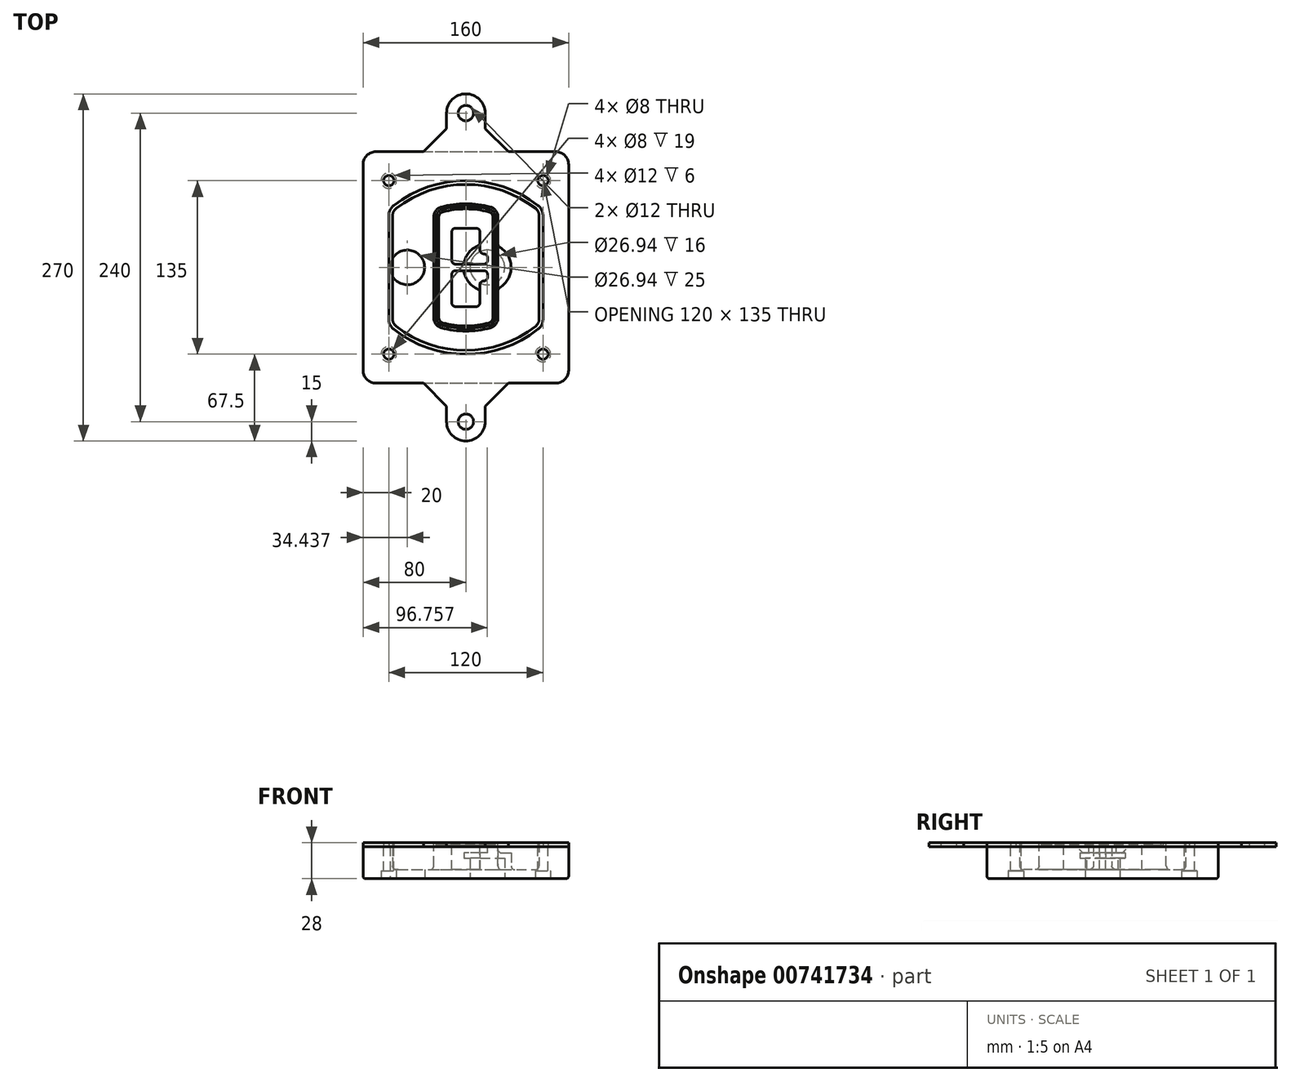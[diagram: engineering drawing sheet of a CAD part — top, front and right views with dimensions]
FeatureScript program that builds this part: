
annotation { "Feature Type Name" : "Feature", "Feature Type Description" : "" }
export const myFeature = defineFeature(function(context is Context, id is Id, definition is map)
    precondition{}
    {
        {
            var Q0;
            Q0=qCreatedBy(makeId("Top.planeOp"),FACE);
            var sketch = newSketch(context, id + "F0", { "sketchPlane" : qUnion([Q0])});
            skPoint(sketch, "E0.rect.middle", {"position": v(0, 0) * mm});
            skLineSegment(sketch, "E1.bottom", {"start": v(-70, -90) * mm, "end": v(70, -90) * mm});
            skLineSegment(sketch, "E1.top", {"start": v(-70, 90) * mm, "end": v(70, 90) * mm});
            skLineSegment(sketch, "E1.left", {"start": v(-80, -80) * mm, "end": v(-80, 80) * mm});
            skLineSegment(sketch, "E1.right", {"start": v(80, -80) * mm, "end": v(80, 80) * mm});
            skLineSegment(sketch, "E2", {"start": v(-80, 90) * mm, "end": v(80, -90) * mm, "construction": true});
            skLineSegment(sketch, "E3", {"start": v(80, 90) * mm, "end": v(-80, -90) * mm, "construction": true});
            skCircle(sketch, "E4", {"center": v(-60, 67.5) * mm, "radius": 4 * mm});
            skCircle(sketch, "E5", {"center": v(60, 67.5) * mm, "radius": 4 * mm});
            skCircle(sketch, "E6", {"center": v(60, -67.5) * mm, "radius": 4 * mm});
            skCircle(sketch, "E7", {"center": v(-60, -67.5) * mm, "radius": 4 * mm});
            skLineSegment(sketch, "E8", {"start": v(-60, 67.5) * mm, "end": v(60, 67.5) * mm, "construction": true});
            skLineSegment(sketch, "E9", {"start": v(60, 67.5) * mm, "end": v(60, -67.5) * mm, "construction": true});
            skLineSegment(sketch, "E10", {"start": v(60, -67.5) * mm, "end": v(-60, -67.5) * mm, "construction": true});
            skLineSegment(sketch, "E11", {"start": v(-60, -67.5) * mm, "end": v(-60, 67.5) * mm, "construction": true});
            skLineSegment(sketch, "E12", {"start": v(-60, 40.3) * mm, "end": v(-60, -40.3) * mm});
            skLineSegment(sketch, "E13", {"start": v(60, 40.3) * mm, "end": v(60, -40.3) * mm});
            skArc(sketch, "E14", {"start": v(56.15, 48.18) * mm, "mid": v(0, 67.5) * mm, "end": v(-56.15, 48.18) * mm});
            skArc(sketch, "E15", {"start": v(-56.15, -48.18) * mm, "mid": v(0, -67.5) * mm, "end": v(56.15, -48.18) * mm});
            skLineSegment(sketch, "E16", {"start": v(-60, 0) * mm, "end": v(60, 0) * mm, "construction": true});
            skPoint(sketch, "E17.visualSharp", {"position": v(-60, -45) * mm});
            skArc(sketch, "E17.filletArc", {"start": v(-60, -40.3) * mm, "mid": v(-58.99, -44.68) * mm, "end": v(-56.15, -48.18) * mm});
            skPoint(sketch, "E18.visualSharp", {"position": v(-60, 45) * mm});
            skArc(sketch, "E18.filletArc", {"start": v(-56.15, 48.18) * mm, "mid": v(-58.99, 44.68) * mm, "end": v(-60, 40.3) * mm});
            skPoint(sketch, "E19.visualSharp", {"position": v(60, 45) * mm});
            skArc(sketch, "E19.filletArc", {"start": v(60, 40.3) * mm, "mid": v(58.99, 44.68) * mm, "end": v(56.15, 48.18) * mm});
            skPoint(sketch, "E20.visualSharp", {"position": v(60, -45) * mm});
            skArc(sketch, "E20.filletArc", {"start": v(56.15, -48.18) * mm, "mid": v(58.99, -44.68) * mm, "end": v(60, -40.3) * mm});
            skPoint(sketch, "E21.visualSharp", {"position": v(-80, 90) * mm});
            skArc(sketch, "E21.filletArc", {"start": v(-70, 90) * mm, "mid": v(-77.07, 87.07) * mm, "end": v(-80, 80) * mm});
            skPoint(sketch, "E22.visualSharp", {"position": v(80, 90) * mm});
            skArc(sketch, "E22.filletArc", {"start": v(80, 80) * mm, "mid": v(77.07, 87.07) * mm, "end": v(70, 90) * mm});
            skPoint(sketch, "E23.visualSharp", {"position": v(80, -90) * mm});
            skArc(sketch, "E23.filletArc", {"start": v(70, -90) * mm, "mid": v(77.07, -87.07) * mm, "end": v(80, -80) * mm});
            skPoint(sketch, "E24.visualSharp", {"position": v(-80, -90) * mm});
            skArc(sketch, "E24.filletArc", {"start": v(-80, -80) * mm, "mid": v(-77.07, -87.07) * mm, "end": v(-70, -90) * mm});
            skArc(sketch, "E25.0", {"start": v(57, 40.3) * mm, "mid": v(56.3, 43.36) * mm, "end": v(54.3, 45.81) * mm});
            skLineSegment(sketch, "E25.1", {"start": v(57, 40.3) * mm, "end": v(57, -40.3) * mm});
            skArc(sketch, "E25.2", {"start": v(54.3, -45.81) * mm, "mid": v(56.3, -43.36) * mm, "end": v(57, -40.3) * mm});
            skArc(sketch, "E25.3", {"start": v(-54.3, -45.81) * mm, "mid": v(0, -64.5) * mm, "end": v(54.3, -45.81) * mm});
            skArc(sketch, "E25.4", {"start": v(-57, -40.3) * mm, "mid": v(-56.3, -43.36) * mm, "end": v(-54.3, -45.81) * mm});
            skArc(sketch, "E25.5", {"start": v(54.3, 45.81) * mm, "mid": v(0, 64.5) * mm, "end": v(-54.3, 45.81) * mm});
            skLineSegment(sketch, "E25.6", {"start": v(-57, 40.3) * mm, "end": v(-57, -40.3) * mm});
            skArc(sketch, "E25.7", {"start": v(-54.3, 45.81) * mm, "mid": v(-56.3, 43.36) * mm, "end": v(-57, 40.3) * mm});
            skArc(sketch, "E26.0", {"start": v(-58.62, 51.33) * mm, "mid": v(-62.58, 46.43) * mm, "end": v(-64, 40.3) * mm});
            skArc(sketch, "E26.1", {"start": v(58.62, 51.33) * mm, "mid": v(0, 71.5) * mm, "end": v(-58.62, 51.33) * mm});
            skArc(sketch, "E26.2", {"start": v(64, 40.3) * mm, "mid": v(62.58, 46.43) * mm, "end": v(58.62, 51.33) * mm});
            skLineSegment(sketch, "E26.3", {"start": v(64, 40.3) * mm, "end": v(64, -40.3) * mm});
            skArc(sketch, "E26.4", {"start": v(58.62, -51.33) * mm, "mid": v(62.58, -46.43) * mm, "end": v(64, -40.3) * mm});
            skLineSegment(sketch, "E26.5", {"start": v(-64, 40.3) * mm, "end": v(-64, -40.3) * mm});
            skArc(sketch, "E26.6", {"start": v(-58.62, -51.33) * mm, "mid": v(0, -71.5) * mm, "end": v(58.62, -51.33) * mm});
            skArc(sketch, "E26.7", {"start": v(-64, -40.3) * mm, "mid": v(-62.58, -46.43) * mm, "end": v(-58.62, -51.33) * mm});
            skSolve(sketch);
        }
        {
            var Q0;
            Q0=makeQuery(id+"F0.imprint","IMPRINT",FACE,{"disambiguationData":[TD([[makeQuery(id+"F0.imprint","IMPRINT",EDGE,{"derivedFrom":sQuery(id+"F0.wireOp",EDGE,"E1.bottom")}),1.0]])]});
            var Q1;
            Q1=makeQuery(id+"F0.imprint","IMPRINT",FACE,{"disambiguationData":[TD([[makeQuery(id+"F0.imprint","IMPRINT",EDGE,{"derivedFrom":sQuery(id+"F0.wireOp",EDGE,"E12")}),1.0]])]});
            var Q2;
            Q2=makeQuery(id+"F0.imprint","IMPRINT",FACE,{"disambiguationData":[TD([[makeQuery(id+"F0.imprint","IMPRINT",EDGE,{"derivedFrom":sQuery(id+"F0.wireOp",EDGE,"E25.0")}),1.0]])]});
            var Q3;
            Q3=makeQuery(id+"F0.imprint","IMPRINT",FACE,{"disambiguationData":[TD([[makeQuery(id+"F0.imprint","IMPRINT",EDGE,{"derivedFrom":sQuery(id+"F0.wireOp",EDGE,"E12")}),-1.0]])]});
            extrude(context, id + "F1", {"entities" : qUnion([Q0, Q1, Q2, Q3]), "oppositeDirection" : true, "depth" : 25 * mm});
        }
        {
            var Q0;
            Q0=makeQuery(id+"F0.imprint","IMPRINT",FACE,{"disambiguationData":[TD([[makeQuery(id+"F0.imprint","IMPRINT",EDGE,{"derivedFrom":sQuery(id+"F0.wireOp",EDGE,"E12")}),1.0]])]});
            extrude(context, id + "F2", {"entities" : qUnion([Q0]), "operationType" : NewBodyOperationType.ADD, "depth" : 3 * mm});
        }
        {
            var Q0;
            Q0=makeQuery(id+"F0.imprint","IMPRINT",FACE,{"disambiguationData":[TD([[makeQuery(id+"F0.imprint","IMPRINT",EDGE,{"derivedFrom":sQuery(id+"F0.wireOp",EDGE,"E25.0")}),1.0]])]});
            extrude(context, id + "F3", {"entities" : qUnion([Q0]), "operationType" : NewBodyOperationType.REMOVE, "oppositeDirection" : true, "depth" : 18 * mm});
        }
        {
            var Q0;
            Q0=makeQuery(id+"F2.opExtrude","CAP_FACE",FACE,{"disambiguationData":[OSD([sQuery(id+"F0.wireOp",EDGE,"E12"),sQuery(id+"F0.wireOp",EDGE,"E13"),sQuery(id+"F0.wireOp",EDGE,"E14"),sQuery(id+"F0.wireOp",EDGE,"E15"),sQuery(id+"F0.wireOp",EDGE,"E17.filletArc"),sQuery(id+"F0.wireOp",EDGE,"E18.filletArc"),sQuery(id+"F0.wireOp",EDGE,"E19.filletArc"),sQuery(id+"F0.wireOp",EDGE,"E20.filletArc"),sQuery(id+"F0.wireOp",EDGE,"E25.0"),sQuery(id+"F0.wireOp",EDGE,"E25.1"),sQuery(id+"F0.wireOp",EDGE,"E25.2"),sQuery(id+"F0.wireOp",EDGE,"E25.3"),sQuery(id+"F0.wireOp",EDGE,"E25.4"),sQuery(id+"F0.wireOp",EDGE,"E25.5"),sQuery(id+"F0.wireOp",EDGE,"E25.6"),sQuery(id+"F0.wireOp",EDGE,"E25.7")])],"isStart":false});
            var sketch = newSketch(context, id + "F4", { "sketchPlane" : qUnion([Q0])});
            skArc(sketch, "E27.0", {"start": v(-19.08, -46.97) * mm, "mid": v(0, -49.5) * mm, "end": v(19.08, -46.97) * mm});
            skArc(sketch, "E28.0", {"start": v(19.08, 46.97) * mm, "mid": v(0, 49.5) * mm, "end": v(-19.08, 46.97) * mm});
            skLineSegment(sketch, "E29", {"start": v(-25, 39.25) * mm, "end": v(-25, -39.25) * mm});
            skLineSegment(sketch, "E30", {"start": v(25, 39.25) * mm, "end": v(25, -39.25) * mm});
            skLineSegment(sketch, "E31", {"start": v(-25, 45.1) * mm, "end": v(25, 45.1) * mm, "construction": true});
            skLineSegment(sketch, "E32", {"start": v(-25, -45.1) * mm, "end": v(25, -45.1) * mm, "construction": true});
            skPoint(sketch, "E33.visualSharp", {"position": v(-25, 45.1) * mm});
            skArc(sketch, "E33.filletArc", {"start": v(-19.08, 46.97) * mm, "mid": v(-23.35, 44.11) * mm, "end": v(-25, 39.25) * mm});
            skPoint(sketch, "E34.visualSharp", {"position": v(25, 45.1) * mm});
            skArc(sketch, "E34.filletArc", {"start": v(25, 39.25) * mm, "mid": v(23.35, 44.11) * mm, "end": v(19.08, 46.97) * mm});
            skPoint(sketch, "E35.visualSharp", {"position": v(25, -45.1) * mm});
            skArc(sketch, "E35.filletArc", {"start": v(19.08, -46.97) * mm, "mid": v(23.35, -44.11) * mm, "end": v(25, -39.25) * mm});
            skPoint(sketch, "E36.visualSharp", {"position": v(-25, -45.1) * mm});
            skArc(sketch, "E36.filletArc", {"start": v(-25, -39.25) * mm, "mid": v(-23.35, -44.11) * mm, "end": v(-19.08, -46.97) * mm});
            skArc(sketch, "E37.0", {"start": v(54.3, 45.81) * mm, "mid": v(0, 64.5) * mm, "end": v(-54.3, 45.81) * mm});
            skArc(sketch, "E37.1", {"start": v(-54.3, 45.81) * mm, "mid": v(-56.3, 43.36) * mm, "end": v(-57, 40.3) * mm});
            skLineSegment(sketch, "E37.2", {"start": v(-57, 40.3) * mm, "end": v(-57, -40.3) * mm});
            skArc(sketch, "E37.3", {"start": v(-57, -40.3) * mm, "mid": v(-56.3, -43.36) * mm, "end": v(-54.3, -45.81) * mm});
            skArc(sketch, "E37.4", {"start": v(-54.3, -45.81) * mm, "mid": v(0, -64.5) * mm, "end": v(54.3, -45.81) * mm});
            skArc(sketch, "E37.5", {"start": v(54.3, -45.81) * mm, "mid": v(56.3, -43.36) * mm, "end": v(57, -40.3) * mm});
            skLineSegment(sketch, "E37.6", {"start": v(57, 40.3) * mm, "end": v(57, -40.3) * mm});
            skArc(sketch, "E37.7", {"start": v(57, 40.3) * mm, "mid": v(56.3, 43.36) * mm, "end": v(54.3, 45.81) * mm});
            skLineSegment(sketch, "E38.0", {"start": v(23, 39.25) * mm, "end": v(23, -39.25) * mm});
            skArc(sketch, "E38.1", {"start": v(18.56, -45.04) * mm, "mid": v(21.76, -42.9) * mm, "end": v(23, -39.25) * mm});
            skArc(sketch, "E38.2", {"start": v(-18.56, -45.04) * mm, "mid": v(0, -47.5) * mm, "end": v(18.56, -45.04) * mm});
            skArc(sketch, "E38.3", {"start": v(-23, -39.25) * mm, "mid": v(-21.76, -42.9) * mm, "end": v(-18.56, -45.04) * mm});
            skLineSegment(sketch, "E38.4", {"start": v(-23, 39.25) * mm, "end": v(-23, -39.25) * mm});
            skArc(sketch, "E38.5", {"start": v(23, 39.25) * mm, "mid": v(21.76, 42.9) * mm, "end": v(18.56, 45.04) * mm});
            skArc(sketch, "E38.6", {"start": v(-18.56, 45.04) * mm, "mid": v(-21.76, 42.9) * mm, "end": v(-23, 39.25) * mm});
            skArc(sketch, "E38.7", {"start": v(18.56, 45.04) * mm, "mid": v(0, 47.5) * mm, "end": v(-18.56, 45.04) * mm});
            skArc(sketch, "E39.0", {"start": v(21, 39.25) * mm, "mid": v(20.18, 41.68) * mm, "end": v(18.04, 43.1) * mm});
            skLineSegment(sketch, "E39.1", {"start": v(21, 39.25) * mm, "end": v(21, -39.25) * mm});
            skArc(sketch, "E39.2", {"start": v(18.04, -43.1) * mm, "mid": v(20.18, -41.68) * mm, "end": v(21, -39.25) * mm});
            skArc(sketch, "E39.3", {"start": v(-18.04, -43.1) * mm, "mid": v(0, -45.5) * mm, "end": v(18.04, -43.1) * mm});
            skArc(sketch, "E39.4", {"start": v(-21, -39.25) * mm, "mid": v(-20.18, -41.68) * mm, "end": v(-18.04, -43.1) * mm});
            skArc(sketch, "E39.5", {"start": v(18.04, 43.1) * mm, "mid": v(0, 45.5) * mm, "end": v(-18.04, 43.1) * mm});
            skLineSegment(sketch, "E39.6", {"start": v(-21, 39.25) * mm, "end": v(-21, -39.25) * mm});
            skArc(sketch, "E39.7", {"start": v(-18.04, 43.1) * mm, "mid": v(-20.18, 41.68) * mm, "end": v(-21, 39.25) * mm});
            skLineSegment(sketch, "E40", {"start": v(-25, 0) * mm, "end": v(25, 0) * mm, "construction": true});
            skLineSegment(sketch, "E41", {"start": v(-11, 5.5) * mm, "end": v(-11, 27.5) * mm});
            skLineSegment(sketch, "E42", {"start": v(-8, 30.5) * mm, "end": v(8, 30.5) * mm});
            skLineSegment(sketch, "E43", {"start": v(11, 27.5) * mm, "end": v(11, 13.5) * mm});
            skLineSegment(sketch, "E44", {"start": v(14, 10.5) * mm, "end": v(14, 10.5) * mm});
            skLineSegment(sketch, "E45", {"start": v(17, 7.5) * mm, "end": v(17, 5.5) * mm});
            skLineSegment(sketch, "E46", {"start": v(14, 2.5) * mm, "end": v(-8, 2.5) * mm});
            skPoint(sketch, "E47.visualSharp", {"position": v(-11, 30.5) * mm});
            skArc(sketch, "E47.filletArc", {"start": v(-8, 30.5) * mm, "mid": v(-10.12, 29.62) * mm, "end": v(-11, 27.5) * mm});
            skPoint(sketch, "E48.visualSharp", {"position": v(11, 30.5) * mm});
            skArc(sketch, "E48.filletArc", {"start": v(11, 27.5) * mm, "mid": v(10.12, 29.62) * mm, "end": v(8, 30.5) * mm});
            skPoint(sketch, "E49.visualSharp", {"position": v(11, 10.5) * mm});
            skArc(sketch, "E49.filletArc", {"start": v(11, 13.5) * mm, "mid": v(11.88, 11.38) * mm, "end": v(14, 10.5) * mm});
            skPoint(sketch, "E50.visualSharp", {"position": v(17, 10.5) * mm});
            skArc(sketch, "E50.filletArc", {"start": v(17, 7.5) * mm, "mid": v(16.12, 9.62) * mm, "end": v(14, 10.5) * mm});
            skPoint(sketch, "E51.visualSharp", {"position": v(17, 2.5) * mm});
            skArc(sketch, "E51.filletArc", {"start": v(14, 2.5) * mm, "mid": v(16.12, 3.38) * mm, "end": v(17, 5.5) * mm});
            skPoint(sketch, "E52.visualSharp", {"position": v(-11, 2.5) * mm});
            skArc(sketch, "E52.filletArc", {"start": v(-11, 5.5) * mm, "mid": v(-10.12, 3.38) * mm, "end": v(-8, 2.5) * mm});
            skLineSegment(sketch, "E53.0.MirrorCS", {"start": v(14, -2.5) * mm, "end": v(-8, -2.5) * mm});
            skArc(sketch, "E54.0.MirrorCS", {"start": v(-11, -5.5) * mm, "mid": v(-10.12, -3.38) * mm, "end": v(-8, -2.5) * mm});
            skLineSegment(sketch, "E55.0.MirrorCS", {"start": v(-11, -5.5) * mm, "end": v(-11, -27.5) * mm});
            skArc(sketch, "E56.0.MirrorCS", {"start": v(-8, -30.5) * mm, "mid": v(-10.12, -29.62) * mm, "end": v(-11, -27.5) * mm});
            skLineSegment(sketch, "E57.0.MirrorCS", {"start": v(-8, -30.5) * mm, "end": v(8, -30.5) * mm});
            skArc(sketch, "E58.0.MirrorCS", {"start": v(11, -27.5) * mm, "mid": v(10.12, -29.62) * mm, "end": v(8, -30.5) * mm});
            skLineSegment(sketch, "E59.0.MirrorCS", {"start": v(11, -27.5) * mm, "end": v(11, -13.5) * mm});
            skArc(sketch, "E60.0.MirrorCS", {"start": v(11, -13.5) * mm, "mid": v(11.88, -11.38) * mm, "end": v(14, -10.5) * mm});
            skArc(sketch, "E61.0.MirrorCS", {"start": v(17, -7.5) * mm, "mid": v(16.12, -9.62) * mm, "end": v(14, -10.5) * mm});
            skLineSegment(sketch, "E62.0.MirrorCS", {"start": v(17, -7.5) * mm, "end": v(17, -5.5) * mm});
            skArc(sketch, "E63.0.MirrorCS", {"start": v(14, -2.5) * mm, "mid": v(16.12, -3.38) * mm, "end": v(17, -5.5) * mm});
            skSolve(sketch);
        }
        {
            var Q0;
            Q0=makeQuery(id+"F4.imprint","IMPRINT",FACE,{"disambiguationData":[TD([[makeQuery(id+"F4.imprint","IMPRINT",EDGE,{"derivedFrom":sQuery(id+"F4.wireOp",EDGE,"E27.0")}),1.0]])]});
            var Q1;
            Q1=makeQuery(id+"F4.imprint","IMPRINT",FACE,{"disambiguationData":[TD([[makeQuery(id+"F4.imprint","IMPRINT",EDGE,{"derivedFrom":sQuery(id+"F4.wireOp",EDGE,"E38.0")}),-1.0]])]});
            var Q2;
            Q2=makeQuery(id+"F4.imprint","IMPRINT",FACE,{"disambiguationData":[TD([[makeQuery(id+"F4.imprint","IMPRINT",EDGE,{"derivedFrom":sQuery(id+"F4.wireOp",EDGE,"E39.0")}),1.0]])]});
            extrude(context, id + "F5", {"entities" : qUnion([Q0, Q1, Q2]), "operationType" : NewBodyOperationType.ADD, "endBound" : BoundingType.UP_TO_NEXT, "oppositeDirection" : true, "depth" : 25 * mm});
        }
        {
            var Q0;
            Q0=makeQuery(id+"F4.imprint","IMPRINT",FACE,{"disambiguationData":[TD([[makeQuery(id+"F4.imprint","IMPRINT",EDGE,{"derivedFrom":sQuery(id+"F4.wireOp",EDGE,"E38.0")}),-1.0]])]});
            extrude(context, id + "F6", {"entities" : qUnion([Q0]), "operationType" : NewBodyOperationType.REMOVE, "oppositeDirection" : true, "depth" : 2 * mm});
        }
        {
            var Q0;
            Q0=makeQuery(id+"F1.opExtrude","CAP_FACE",FACE,{"disambiguationData":[OSD([sQuery(id+"F0.wireOp",EDGE,"E1.bottom"),sQuery(id+"F0.wireOp",EDGE,"E1.top"),sQuery(id+"F0.wireOp",EDGE,"E1.left"),sQuery(id+"F0.wireOp",EDGE,"E1.right"),sQuery(id+"F0.wireOp",EDGE,"E4"),sQuery(id+"F0.wireOp",EDGE,"E5"),sQuery(id+"F0.wireOp",EDGE,"E6"),sQuery(id+"F0.wireOp",EDGE,"E7"),sQuery(id+"F0.wireOp",EDGE,"E21.filletArc"),sQuery(id+"F0.wireOp",EDGE,"E22.filletArc"),sQuery(id+"F0.wireOp",EDGE,"E23.filletArc"),sQuery(id+"F0.wireOp",EDGE,"E24.filletArc")])],"isStart":false});
            var sketch = newSketch(context, id + "F7", { "sketchPlane" : qUnion([Q0])});
            skCircle(sketch, "E64", {"center": v(16.76, 0) * mm, "radius": 13.47 * mm});
            skCircle(sketch, "E65", {"center": v(-45.56, 0) * mm, "radius": 13.47 * mm});
            skLineSegment(sketch, "E66", {"start": v(80, 0) * mm, "end": v(-80, 0) * mm});
            skCircle(sketch, "E67", {"center": v(16.76, 0) * mm, "radius": 18.47 * mm});
            skCircle(sketch, "E68", {"center": v(60, -67.5) * mm, "radius": 6 * mm});
            skCircle(sketch, "E69", {"center": v(-60, -67.5) * mm, "radius": 6 * mm});
            skCircle(sketch, "E70", {"center": v(-60, 67.5) * mm, "radius": 6 * mm});
            skCircle(sketch, "E71", {"center": v(60, 67.5) * mm, "radius": 6 * mm});
            skSolve(sketch);
        }
        {
            var Q0;
            {var subQ1=sQuery(id+"F7.wireOp",EDGE,"E66");var subQ4=sQuery(id+"F7.wireOp",EDGE,"E64");var subQ6=makeQuery(id+"F7.imprint","INTERSECT",VERTEX,{"disambiguationData":[OD(0.0)],"derivedFrom":[subQ4,subQ1]});Q0=makeQuery(id+"F7.imprint","IMPRINT",FACE,{"disambiguationData":[TD([[makeQuery(id+"F7.imprint","IMPRINT",EDGE,{"disambiguationData":[TD([[subQ6,-1.0]])],"derivedFrom":subQ4}),-1.0]])]});}
            var Q1;
            {var subQ0=sQuery(id+"F7.wireOp",EDGE,"E66");var subQ1=sQuery(id+"F7.wireOp",EDGE,"E64");var subQ3=makeQuery(id+"F7.imprint","INTERSECT",VERTEX,{"disambiguationData":[OD(0.0)],"derivedFrom":[subQ1,subQ0]});Q1=makeQuery(id+"F7.imprint","IMPRINT",FACE,{"disambiguationData":[TD([[makeQuery(id+"F7.imprint","IMPRINT",EDGE,{"disambiguationData":[TD([[subQ3,-1.0]])],"derivedFrom":subQ1}),1.0]])]});}
            var Q2;
            {var subQ0=sQuery(id+"F7.wireOp",EDGE,"E66");var subQ1=sQuery(id+"F7.wireOp",EDGE,"E64");var subQ3=makeQuery(id+"F7.imprint","INTERSECT",VERTEX,{"disambiguationData":[OD(0.0)],"derivedFrom":[subQ1,subQ0]});Q2=makeQuery(id+"F7.imprint","IMPRINT",FACE,{"disambiguationData":[TD([[makeQuery(id+"F7.imprint","IMPRINT",EDGE,{"disambiguationData":[TD([[subQ3,1.0]])],"derivedFrom":subQ1}),1.0]])]});}
            var Q3;
            {var subQ1=sQuery(id+"F7.wireOp",EDGE,"E66");var subQ4=sQuery(id+"F7.wireOp",EDGE,"E64");var subQ6=makeQuery(id+"F7.imprint","INTERSECT",VERTEX,{"disambiguationData":[OD(0.0)],"derivedFrom":[subQ4,subQ1]});Q3=makeQuery(id+"F7.imprint","IMPRINT",FACE,{"disambiguationData":[TD([[makeQuery(id+"F7.imprint","IMPRINT",EDGE,{"disambiguationData":[TD([[subQ6,1.0]])],"derivedFrom":subQ4}),-1.0]])]});}
            extrude(context, id + "F8", {"entities" : qUnion([Q0, Q1, Q2, Q3]), "operationType" : NewBodyOperationType.ADD, "oppositeDirection" : true, "depth" : 20 * mm});
        }
        {
            var Q0;
            {var subQ0=sQuery(id+"F7.wireOp",EDGE,"E66");var subQ1=sQuery(id+"F7.wireOp",EDGE,"E64");var subQ3=makeQuery(id+"F7.imprint","INTERSECT",VERTEX,{"disambiguationData":[OD(0.0)],"derivedFrom":[subQ1,subQ0]});Q0=makeQuery(id+"F7.imprint","IMPRINT",FACE,{"disambiguationData":[TD([[makeQuery(id+"F7.imprint","IMPRINT",EDGE,{"disambiguationData":[TD([[subQ3,-1.0]])],"derivedFrom":subQ1}),1.0]])]});}
            var Q1;
            {var subQ0=sQuery(id+"F7.wireOp",EDGE,"E66");var subQ1=sQuery(id+"F7.wireOp",EDGE,"E64");var subQ3=makeQuery(id+"F7.imprint","INTERSECT",VERTEX,{"disambiguationData":[OD(0.0)],"derivedFrom":[subQ1,subQ0]});Q1=makeQuery(id+"F7.imprint","IMPRINT",FACE,{"disambiguationData":[TD([[makeQuery(id+"F7.imprint","IMPRINT",EDGE,{"disambiguationData":[TD([[subQ3,1.0]])],"derivedFrom":subQ1}),1.0]])]});}
            extrude(context, id + "F9", {"entities" : qUnion([Q0, Q1]), "operationType" : NewBodyOperationType.REMOVE, "oppositeDirection" : true, "depth" : 16 * mm});
        }
        {
            var Q0;
            {var subQ0=sQuery(id+"F7.wireOp",EDGE,"E66");var subQ1=sQuery(id+"F7.wireOp",EDGE,"E65");var subQ3=makeQuery(id+"F7.imprint","INTERSECT",VERTEX,{"disambiguationData":[OD(0.0)],"derivedFrom":[subQ1,subQ0]});Q0=makeQuery(id+"F7.imprint","IMPRINT",FACE,{"disambiguationData":[TD([[makeQuery(id+"F7.imprint","IMPRINT",EDGE,{"disambiguationData":[TD([[subQ3,-1.0]])],"derivedFrom":subQ1}),1.0]])]});}
            var Q1;
            {var subQ0=sQuery(id+"F7.wireOp",EDGE,"E66");var subQ1=sQuery(id+"F7.wireOp",EDGE,"E65");var subQ3=makeQuery(id+"F7.imprint","INTERSECT",VERTEX,{"disambiguationData":[OD(0.0)],"derivedFrom":[subQ1,subQ0]});Q1=makeQuery(id+"F7.imprint","IMPRINT",FACE,{"disambiguationData":[TD([[makeQuery(id+"F7.imprint","IMPRINT",EDGE,{"disambiguationData":[TD([[subQ3,1.0]])],"derivedFrom":subQ1}),1.0]])]});}
            extrude(context, id + "F10", {"entities" : qUnion([Q0, Q1]), "operationType" : NewBodyOperationType.REMOVE, "oppositeDirection" : true, "depth" : 25 * mm});
        }
        {
            var Q0;
            Q0=makeQuery(id+"F7.imprint","IMPRINT",FACE,{"disambiguationData":[TD([[makeQuery(id+"F7.imprint","IMPRINT",EDGE,{"derivedFrom":sQuery(id+"F7.wireOp",EDGE,"E68")}),1.0]])]});
            var Q1;
            Q1=makeQuery(id+"F7.imprint","IMPRINT",FACE,{"disambiguationData":[TD([[makeQuery(id+"F7.imprint","IMPRINT",EDGE,{"derivedFrom":makeQuery(id+"F1.opExtrude","CAP_EDGE",EDGE,{"disambiguationData":[OSD([sQuery(id+"F0.wireOp",EDGE,"E5")])],"isStart":false})}),-1.0]])]});
            var Q2;
            Q2=makeQuery(id+"F7.imprint","IMPRINT",FACE,{"disambiguationData":[TD([[makeQuery(id+"F7.imprint","IMPRINT",EDGE,{"derivedFrom":sQuery(id+"F7.wireOp",EDGE,"E69")}),1.0]])]});
            var Q3;
            Q3=makeQuery(id+"F7.imprint","IMPRINT",FACE,{"disambiguationData":[TD([[makeQuery(id+"F7.imprint","IMPRINT",EDGE,{"derivedFrom":makeQuery(id+"F1.opExtrude","CAP_EDGE",EDGE,{"disambiguationData":[OSD([sQuery(id+"F0.wireOp",EDGE,"E4")])],"isStart":false})}),-1.0]])]});
            var Q4;
            Q4=makeQuery(id+"F7.imprint","IMPRINT",FACE,{"disambiguationData":[TD([[makeQuery(id+"F7.imprint","IMPRINT",EDGE,{"derivedFrom":sQuery(id+"F7.wireOp",EDGE,"E70")}),1.0]])]});
            var Q5;
            Q5=makeQuery(id+"F7.imprint","IMPRINT",FACE,{"disambiguationData":[TD([[makeQuery(id+"F7.imprint","IMPRINT",EDGE,{"derivedFrom":makeQuery(id+"F1.opExtrude","CAP_EDGE",EDGE,{"disambiguationData":[OSD([sQuery(id+"F0.wireOp",EDGE,"E7")])],"isStart":false})}),-1.0]])]});
            var Q6;
            Q6=makeQuery(id+"F7.imprint","IMPRINT",FACE,{"disambiguationData":[TD([[makeQuery(id+"F7.imprint","IMPRINT",EDGE,{"derivedFrom":sQuery(id+"F7.wireOp",EDGE,"E71")}),1.0]])]});
            var Q7;
            Q7=makeQuery(id+"F7.imprint","IMPRINT",FACE,{"disambiguationData":[TD([[makeQuery(id+"F7.imprint","IMPRINT",EDGE,{"derivedFrom":makeQuery(id+"F1.opExtrude","CAP_EDGE",EDGE,{"disambiguationData":[OSD([sQuery(id+"F0.wireOp",EDGE,"E6")])],"isStart":false})}),-1.0]])]});
            extrude(context, id + "F11", {"entities" : qUnion([Q0, Q1, Q2, Q3, Q4, Q5, Q6, Q7]), "operationType" : NewBodyOperationType.REMOVE, "oppositeDirection" : true, "depth" : 6 * mm});
        }
        {
            var Q0;
            Q0=makeQuery(id+"F9.boolean.opBoolean","COPY",FACE,{"derivedFrom":makeQuery(id+"F9.opExtrude","CAP_FACE",FACE,{"disambiguationData":[OSD([sQuery(id+"F7.wireOp",EDGE,"E64")])],"isStart":false})});
            var sketch = newSketch(context, id + "F12", { "sketchPlane" : qUnion([Q0])});
            skArc(sketch, "E72.0", {"start": v(11, 17.55) * mm, "mid": v(2.57, 11.82) * mm, "end": v(-1.54, 2.5) * mm});
            skArc(sketch, "E72.1", {"start": v(-1.54, -2.5) * mm, "mid": v(2.57, -11.82) * mm, "end": v(11, -17.55) * mm});
            skLineSegment(sketch, "E73", {"start": v(-1.54, -2.5) * mm, "end": v(14, -2.5) * mm});
            skLineSegment(sketch, "E74.0", {"start": v(14, 2.5) * mm, "end": v(-1.54, 2.5) * mm});
            skArc(sketch, "E74.1", {"start": v(14, 2.5) * mm, "mid": v(16.12, 3.38) * mm, "end": v(17, 5.5) * mm});
            skLineSegment(sketch, "E74.2", {"start": v(17, 7.5) * mm, "end": v(17, 5.5) * mm});
            skArc(sketch, "E74.3", {"start": v(17, 7.5) * mm, "mid": v(16.12, 9.62) * mm, "end": v(14, 10.5) * mm});
            skArc(sketch, "E74.4", {"start": v(11, 13.5) * mm, "mid": v(11.88, 11.38) * mm, "end": v(14, 10.5) * mm});
            skLineSegment(sketch, "E74.5", {"start": v(11, 17.55) * mm, "end": v(11, 13.5) * mm});
            skLineSegment(sketch, "E74.7", {"start": v(14, -2.5) * mm, "end": v(-1.54, -2.5) * mm});
            skArc(sketch, "E74.8", {"start": v(14, -2.5) * mm, "mid": v(16.12, -3.38) * mm, "end": v(17, -5.5) * mm});
            skLineSegment(sketch, "E74.9", {"start": v(17, -7.5) * mm, "end": v(17, -5.5) * mm});
            skArc(sketch, "E74.10", {"start": v(17, -7.5) * mm, "mid": v(16.12, -9.62) * mm, "end": v(14, -10.5) * mm});
            skArc(sketch, "E74.11", {"start": v(11, -13.5) * mm, "mid": v(11.88, -11.38) * mm, "end": v(14, -10.5) * mm});
            skLineSegment(sketch, "E74.12", {"start": v(11, -17.55) * mm, "end": v(11, -13.5) * mm});
            skPoint(sketch, "E75.orphan", {"position": v(11, -27.5) * mm});
            skPoint(sketch, "E76.orphan", {"position": v(-8, -2.5) * mm});
            skPoint(sketch, "E77.orphan", {"position": v(-8, 2.5) * mm});
            skPoint(sketch, "E78.orphan", {"position": v(11, 27.5) * mm});
            skSolve(sketch);
        }
        {
            var Q0;
            {var subQ7=sQuery(id+"F12.wireOp",EDGE,"E72.0");var subQ14=sQuery(id+"F12.wireOp",EDGE,"E72.1");var subQ16=sQuery(id+"F12.wireOp",EDGE,"E74.1");var subQ18=sQuery(id+"F12.wireOp",EDGE,"E74.8");Q0=qUnion([makeQuery(id+"F12.imprint","IMPRINT",FACE,{"disambiguationData":[TD([[makeQuery(id+"F12.imprint","IMPRINT",EDGE,{"derivedFrom":subQ7}),1.0]])]}),makeQuery(id+"F12.imprint","IMPRINT",FACE,{"disambiguationData":[TD([[makeQuery(id+"F12.imprint","IMPRINT",EDGE,{"derivedFrom":subQ14}),1.0]])]}),makeQuery(id+"F12.imprint","IMPRINT",FACE,{"disambiguationData":[TD([[makeQuery(id+"F12.imprint","IMPRINT",EDGE,{"derivedFrom":subQ16}),1.0]])]}),makeQuery(id+"F12.imprint","IMPRINT",FACE,{"disambiguationData":[TD([[makeQuery(id+"F12.imprint","IMPRINT",EDGE,{"derivedFrom":subQ18}),-1.0]])]})]);}
            var Q1;
            Q1=makeQuery(id+"F5.boolean.opBoolean","SPLIT",FACE,{"disambiguationData":[TD([makeQuery(id+"F5.opExtrude","SWEPT_FACE",FACE,{"disambiguationData":[OSD([sQuery(id+"F4.wireOp",EDGE,"E41")])]})])],"derivedFrom":makeQuery(id+"F3.boolean.opBoolean","COPY",FACE,{"derivedFrom":makeQuery(id+"F3.opExtrude","CAP_FACE",FACE,{"disambiguationData":[OSD([sQuery(id+"F0.wireOp",EDGE,"E25.0"),sQuery(id+"F0.wireOp",EDGE,"E25.1"),sQuery(id+"F0.wireOp",EDGE,"E25.2"),sQuery(id+"F0.wireOp",EDGE,"E25.3"),sQuery(id+"F0.wireOp",EDGE,"E25.4"),sQuery(id+"F0.wireOp",EDGE,"E25.5"),sQuery(id+"F0.wireOp",EDGE,"E25.6"),sQuery(id+"F0.wireOp",EDGE,"E25.7")])],"isStart":false})})});
            extrude(context, id + "F13", {"entities" : qUnion([Q0]), "operationType" : NewBodyOperationType.REMOVE, "endBound" : BoundingType.UP_TO_SURFACE, "endBoundEntityFace" : qUnion([Q1]), "depth" : 25 * mm});
        }
        {
            var Q0;
            Q0=makeQuery(id+"F3.boolean.opBoolean","COPY",EDGE,{"derivedFrom":makeQuery(id+"F3.opExtrude","CAP_EDGE",EDGE,{"disambiguationData":[OSD([sQuery(id+"F0.wireOp",EDGE,"E25.6")])],"isStart":false})});
            var Q1;
            Q1=makeQuery(id+"F8.boolean.opBoolean","INTERSECT",EDGE,{"derivedFrom":[makeQuery(id+"F5.opExtrude","SWEPT_FACE",FACE,{"disambiguationData":[OSD([sQuery(id+"F4.wireOp",EDGE,"E30")])]}),makeQuery(id+"F8.opExtrude","CAP_FACE",FACE,{"disambiguationData":[OSD([sQuery(id+"F7.wireOp",EDGE,"E67")])],"isStart":false})]});
            var Q2;
            Q2=makeQuery(id+"F8.boolean.opBoolean","INTERSECT",EDGE,{"disambiguationData":[OD(1.0)],"derivedFrom":[makeQuery(id+"F5.opExtrude","SWEPT_FACE",FACE,{"disambiguationData":[OSD([sQuery(id+"F4.wireOp",EDGE,"E30")])]}),makeQuery(id+"F8.opExtrude","SWEPT_FACE",FACE,{"disambiguationData":[OSD([sQuery(id+"F7.wireOp",EDGE,"E67")])]})]});
            var Q3;
            {var subQ0=sQuery(id+"F4.wireOp",EDGE,"E30");Q3=makeQuery(id+"F8.boolean.opBoolean","SPLIT",EDGE,{"disambiguationData":[TD([makeQuery(id+"F5.opExtrude","SWEPT_FACE",FACE,{"disambiguationData":[OSD([sQuery(id+"F4.wireOp",EDGE,"E35.filletArc")])]})])],"derivedFrom":makeQuery(id+"F5.opExtrude","CAP_EDGE",EDGE,{"disambiguationData":[OSD([subQ0])],"isStart":false})});}
            var Q4;
            {var subQ0=sQuery(id+"F0.wireOp",EDGE,"E25.7");var subQ1=sQuery(id+"F0.wireOp",EDGE,"E25.1");var subQ2=sQuery(id+"F0.wireOp",EDGE,"E25.6");var subQ3=sQuery(id+"F0.wireOp",EDGE,"E25.5");var subQ4=sQuery(id+"F0.wireOp",EDGE,"E25.4");var subQ5=sQuery(id+"F0.wireOp",EDGE,"E25.0");var subQ6=sQuery(id+"F0.wireOp",EDGE,"E25.2");var subQ7=sQuery(id+"F0.wireOp",EDGE,"E25.3");Q4=makeQuery(id+"F8.boolean.opBoolean","INTERSECT",EDGE,{"derivedFrom":[makeQuery(id+"F5.boolean.opBoolean","SPLIT",FACE,{"disambiguationData":[TD([makeQuery(id+"F2.opExtrude","SWEPT_FACE",FACE,{"disambiguationData":[OSD([subQ5])]})])],"derivedFrom":makeQuery(id+"F3.boolean.opBoolean","COPY",FACE,{"derivedFrom":makeQuery(id+"F3.opExtrude","CAP_FACE",FACE,{"disambiguationData":[OSD([subQ5,subQ1,subQ6,subQ7,subQ4,subQ3,subQ2,subQ0])],"isStart":false})})}),makeQuery(id+"F8.opExtrude","SWEPT_FACE",FACE,{"disambiguationData":[OSD([sQuery(id+"F7.wireOp",EDGE,"E67")])]})]});}
            var Q5;
            Q5=makeQuery(id+"F8.boolean.opBoolean","INTERSECT",EDGE,{"disambiguationData":[OD(0.0)],"derivedFrom":[makeQuery(id+"F5.opExtrude","SWEPT_FACE",FACE,{"disambiguationData":[OSD([sQuery(id+"F4.wireOp",EDGE,"E30")])]}),makeQuery(id+"F8.opExtrude","SWEPT_FACE",FACE,{"disambiguationData":[OSD([sQuery(id+"F7.wireOp",EDGE,"E67")])]})]});
            fillet(context, id + "F14", {"entities" : qUnion([Q0, Q1, Q2, Q3, Q4, Q5]), "radius" : 3 * mm, "tangentPropagation" : true, "allowEdgeOverflow" : false});
        }
        {
            var Q0;
            Q0=makeQuery(id+"F1.opExtrude","CAP_EDGE",EDGE,{"disambiguationData":[OSD([sQuery(id+"F0.wireOp",EDGE,"E1.bottom")])],"isStart":false});
            fillet(context, id + "F15", {"entities" : qUnion([Q0]), "radius" : 2 * mm, "tangentPropagation" : true, "allowEdgeOverflow" : false});
        }
        {
            var Q0;
            {var subQ0=sQuery(id+"F0.wireOp",EDGE,"E21.filletArc");var subQ1=sQuery(id+"F0.wireOp",EDGE,"E7");var subQ2=sQuery(id+"F0.wireOp",EDGE,"E6");var subQ3=sQuery(id+"F0.wireOp",EDGE,"E5");var subQ4=sQuery(id+"F0.wireOp",EDGE,"E4");var subQ5=sQuery(id+"F0.wireOp",EDGE,"E22.filletArc");var subQ6=sQuery(id+"F0.wireOp",EDGE,"E1.bottom");var subQ7=sQuery(id+"F0.wireOp",EDGE,"E1.right");var subQ8=sQuery(id+"F0.wireOp",EDGE,"E1.top");var subQ9=sQuery(id+"F0.wireOp",EDGE,"E1.left");var subQ10=sQuery(id+"F0.wireOp",EDGE,"E23.filletArc");var subQ11=sQuery(id+"F0.wireOp",EDGE,"E24.filletArc");Q0=makeQuery(id+"F2.boolean.opBoolean","SPLIT",FACE,{"disambiguationData":[TD([makeQuery(id+"F1.opExtrude","SWEPT_FACE",FACE,{"disambiguationData":[OSD([subQ6])]})])],"derivedFrom":makeQuery(id+"F1.opExtrude","CAP_FACE",FACE,{"disambiguationData":[OSD([subQ6,subQ8,subQ9,subQ7,subQ4,subQ3,subQ2,subQ1,subQ0,subQ5,subQ10,subQ11])],"isStart":true})});}
            var sketch = newSketch(context, id + "F16", { "sketchPlane" : qUnion([Q0])});
            skLineSegment(sketch, "E79.0", {"start": v(-80, -80) * mm, "end": v(-80, 80) * mm});
            skArc(sketch, "E79.1", {"start": v(-70, 90) * mm, "mid": v(-77.07, 87.07) * mm, "end": v(-80, 80) * mm});
            skLineSegment(sketch, "E79.2", {"start": v(-70, 90) * mm, "end": v(70, 90) * mm});
            skArc(sketch, "E79.3", {"start": v(56.15, 48.18) * mm, "mid": v(0, 67.5) * mm, "end": v(-56.15, 48.18) * mm});
            skLineSegment(sketch, "E79.4", {"start": v(-60, 40.3) * mm, "end": v(-60, -40.3) * mm});
            skArc(sketch, "E79.5", {"start": v(-56.15, 48.18) * mm, "mid": v(-58.99, 44.68) * mm, "end": v(-60, 40.3) * mm});
            skCircle(sketch, "E79.6", {"center": v(-60, 67.5) * mm, "radius": 4 * mm});
            skCircle(sketch, "E79.7", {"center": v(60, 67.5) * mm, "radius": 4 * mm});
            skLineSegment(sketch, "E79.8", {"start": v(80, -80) * mm, "end": v(80, 80) * mm});
            skArc(sketch, "E79.9", {"start": v(80, 80) * mm, "mid": v(77.07, 87.07) * mm, "end": v(70, 90) * mm});
            skArc(sketch, "E79.10", {"start": v(70, -90) * mm, "mid": v(77.07, -87.07) * mm, "end": v(80, -80) * mm});
            skCircle(sketch, "E79.11", {"center": v(60, -67.5) * mm, "radius": 4 * mm});
            skCircle(sketch, "E79.12", {"center": v(-60, -67.5) * mm, "radius": 4 * mm});
            skArc(sketch, "E79.13", {"start": v(-60, -40.3) * mm, "mid": v(-58.99, -44.68) * mm, "end": v(-56.15, -48.18) * mm});
            skArc(sketch, "E79.14", {"start": v(-56.15, -48.18) * mm, "mid": v(0, -67.5) * mm, "end": v(56.15, -48.18) * mm});
            skArc(sketch, "E79.15", {"start": v(56.15, -48.18) * mm, "mid": v(58.99, -44.68) * mm, "end": v(60, -40.3) * mm});
            skLineSegment(sketch, "E79.16", {"start": v(60, 40.3) * mm, "end": v(60, -40.3) * mm});
            skArc(sketch, "E79.17", {"start": v(60, 40.3) * mm, "mid": v(58.99, 44.68) * mm, "end": v(56.15, 48.18) * mm});
            skLineSegment(sketch, "E79.18", {"start": v(-70, -90) * mm, "end": v(70, -90) * mm});
            skArc(sketch, "E79.19", {"start": v(-80, -80) * mm, "mid": v(-77.07, -87.07) * mm, "end": v(-70, -90) * mm});
            skPoint(sketch, "E80.centerSnap0", {"position": v(0, 90) * mm});
            skLineSegment(sketch, "E81", {"start": v(0, 120) * mm, "end": v(0, 90) * mm, "construction": true});
            skLineSegment(sketch, "E82", {"start": v(-33, 90) * mm, "end": v(-15, 108) * mm});
            skLineSegment(sketch, "E83", {"start": v(-15, 108) * mm, "end": v(-15, 120) * mm});
            skLineSegment(sketch, "E84", {"start": v(33, 90) * mm, "end": v(15, 108) * mm});
            skLineSegment(sketch, "E85", {"start": v(15, 108) * mm, "end": v(15, 120) * mm});
            skArc(sketch, "E86", {"start": v(15, 120) * mm, "mid": v(0, 135) * mm, "end": v(-15, 120) * mm});
            skCircle(sketch, "E87", {"center": v(0, 120) * mm, "radius": 6 * mm});
            skLineSegment(sketch, "E88", {"start": v(-80, 0) * mm, "end": v(80, 0) * mm, "construction": true});
            skLineSegment(sketch, "E89.MirrorCS", {"start": v(-33, -90) * mm, "end": v(-15, -108) * mm});
            skLineSegment(sketch, "E90.MirrorCS", {"start": v(-15, -108) * mm, "end": v(-15, -120) * mm});
            skArc(sketch, "E91.MirrorCS", {"start": v(15, -120) * mm, "mid": v(0, -135) * mm, "end": v(-15, -120) * mm});
            skLineSegment(sketch, "E92.MirrorCS", {"start": v(15, -108) * mm, "end": v(15, -120) * mm});
            skLineSegment(sketch, "E93.MirrorCS", {"start": v(33, -90) * mm, "end": v(15, -108) * mm});
            skCircle(sketch, "E94.MirrorC", {"center": v(0, -120) * mm, "radius": 6 * mm});
            skLineSegment(sketch, "E95.MirrorCS", {"start": v(0, -120) * mm, "end": v(0, -90) * mm, "construction": true});
            skSolve(sketch);
        }
        {
            var Q0;
            Q0 = qSketchRegion(id + "F16", true);
            var Q1;
            Q1=makeQuery(id+"F2.opExtrude","CAP_FACE",FACE,{"disambiguationData":[OSD([sQuery(id+"F0.wireOp",EDGE,"E12"),sQuery(id+"F0.wireOp",EDGE,"E13"),sQuery(id+"F0.wireOp",EDGE,"E14"),sQuery(id+"F0.wireOp",EDGE,"E15"),sQuery(id+"F0.wireOp",EDGE,"E17.filletArc"),sQuery(id+"F0.wireOp",EDGE,"E18.filletArc"),sQuery(id+"F0.wireOp",EDGE,"E19.filletArc"),sQuery(id+"F0.wireOp",EDGE,"E20.filletArc"),sQuery(id+"F0.wireOp",EDGE,"E25.0"),sQuery(id+"F0.wireOp",EDGE,"E25.1"),sQuery(id+"F0.wireOp",EDGE,"E25.2"),sQuery(id+"F0.wireOp",EDGE,"E25.3"),sQuery(id+"F0.wireOp",EDGE,"E25.4"),sQuery(id+"F0.wireOp",EDGE,"E25.5"),sQuery(id+"F0.wireOp",EDGE,"E25.6"),sQuery(id+"F0.wireOp",EDGE,"E25.7")])],"isStart":false});
            extrude(context, id + "F17", {"entities" : qUnion([Q0]), "endBound" : BoundingType.UP_TO_SURFACE, "depth" : 25 * mm, "endBoundEntityFace" : qUnion([Q1]), "offsetDistance" : 25 * mm});
        }
    });
